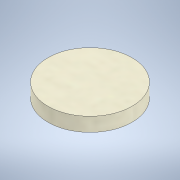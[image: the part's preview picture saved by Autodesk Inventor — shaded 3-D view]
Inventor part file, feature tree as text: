
AUTODESK INVENTOR PART (.ipt)
format: ipt  version: 2021 (Build 250183000, 183)  size: 98,816 bytes
history: native  units: mm
features: extrude x1, sketch x1
ambient origin geometry x8: Origin, YZ Plane, XZ Plane, XY Plane, X Axis, Y Axis, Z Axis, Center Point
bodies: Solid1 (feature_tree)
feature tree (2):
  extrude  "Extrusion1"  Depth=5.25mm TaperAngle=0.0deg
  sketch  "Sketch1"  dims[d0=31.7mm d1=5.25mm d2=0.0mm]
